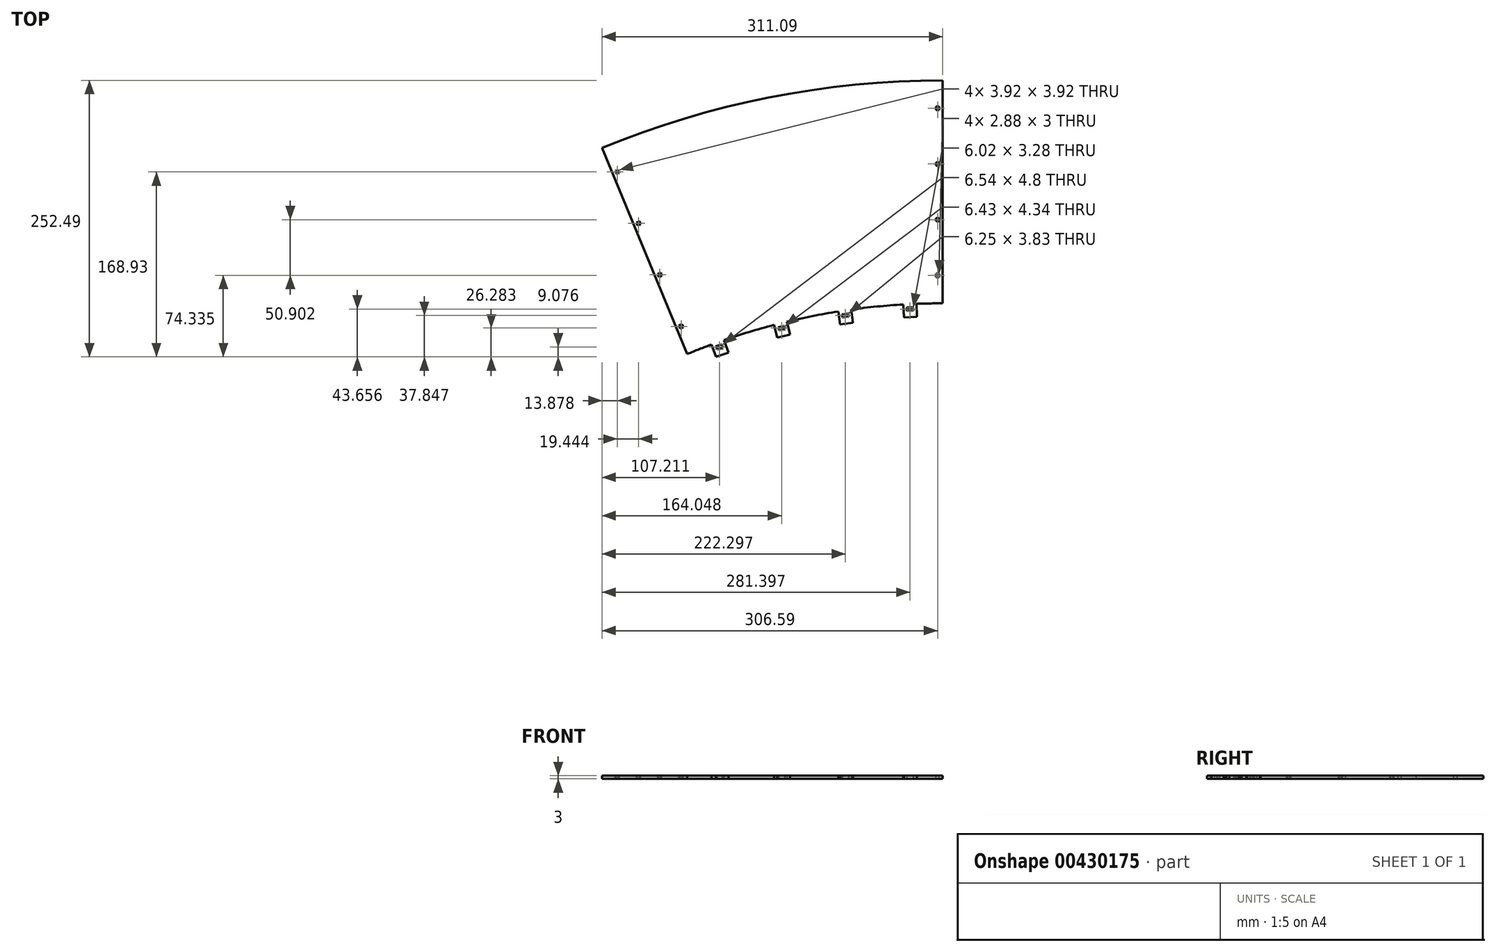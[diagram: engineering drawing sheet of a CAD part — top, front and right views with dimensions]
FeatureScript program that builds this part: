
annotation { "Feature Type Name" : "Feature", "Feature Type Description" : "" }
export const myFeature = defineFeature(function(context is Context, id is Id, definition is map)
    precondition{}
    {
        {
            var Q0;
            Q0=qCreatedBy(makeId("Top.planeOp"),FACE);
            var sketch = newSketch(context, id + "F0", { "sketchPlane" : qUnion([Q0])});
            skLineSegment(sketch, "E0", {"start": v(0, 0) * mm, "end": v(0, 610.8) * mm, "construction": true});
            skLineSegment(sketch, "E1", {"start": v(0, 814.4) * mm, "end": v(0, 610.8) * mm});
            skPoint(sketch, "E2.center", {"position": v(0, 0) * mm});
            skLineSegment(sketch, "E3.1.0", {"start": v(-39.88, 813.42) * mm, "end": v(-29.33, 598.08) * mm, "construction": true});
            skLineSegment(sketch, "E3.anchor2", {"start": v(0, 0) * mm, "end": v(-233.32, 564.48) * mm, "construction": true});
            skArc(sketch, "E4", {"start": v(0, 610.8) * mm, "mid": v(-118.94, 599.1) * mm, "end": v(-233.32, 564.48) * mm});
            skArc(sketch, "E5", {"start": v(0, 814.4) * mm, "mid": v(-158.58, 798.81) * mm, "end": v(-311.1, 752.64) * mm});
            skLineSegment(sketch, "E6.2.2.0", {"start": v(-79.67, 810.5) * mm, "end": v(-59.75, 607.86) * mm, "construction": true});
            skLineSegment(sketch, "E6.2.3.0", {"start": v(-119.27, 805.62) * mm, "end": v(-89.45, 604.2) * mm, "construction": true});
            skLineSegment(sketch, "E6.2.4.0", {"start": v(-158.58, 798.81) * mm, "end": v(-118.94, 599.1) * mm, "construction": true});
            skLineSegment(sketch, "E6.2.5.0", {"start": v(-197.51, 790.09) * mm, "end": v(-148.13, 592.56) * mm, "construction": true});
            skLineSegment(sketch, "E6.2.6.0", {"start": v(-235.97, 779.47) * mm, "end": v(-176.98, 584.6) * mm, "construction": true});
            skLineSegment(sketch, "E6.2.7.0", {"start": v(-273.86, 766.97) * mm, "end": v(-205.4, 575.22) * mm, "construction": true});
            skLineSegment(sketch, "E6.2.8.0", {"start": v(-311.1, 752.64) * mm, "end": v(-233.32, 564.48) * mm});
            skLineSegment(sketch, "E7.bottom", {"start": v(-35.9, 609.77) * mm, "end": v(-23.92, 610.35) * mm});
            skLineSegment(sketch, "E7.top", {"start": v(-35.32, 597.78) * mm, "end": v(-23.33, 598.37) * mm});
            skLineSegment(sketch, "E7.left", {"start": v(-35.9, 609.77) * mm, "end": v(-35.32, 597.78) * mm});
            skLineSegment(sketch, "E7.right", {"start": v(-23.92, 610.35) * mm, "end": v(-23.33, 598.37) * mm});
            skPoint(sketch, "E8.orphan", {"position": v(-29.91, 610.06) * mm});
            skLineSegment(sketch, "E9.bottom", {"start": v(-26.77, 607.21) * mm, "end": v(-32.76, 606.92) * mm, "construction": true});
            skLineSegment(sketch, "E9.top", {"start": v(-26.62, 604.22) * mm, "end": v(-32.62, 603.92) * mm, "construction": true});
            skLineSegment(sketch, "E9.left", {"start": v(-26.77, 607.21) * mm, "end": v(-26.62, 604.22) * mm, "construction": true});
            skLineSegment(sketch, "E9.right", {"start": v(-32.76, 606.92) * mm, "end": v(-32.62, 603.92) * mm, "construction": true});
            skPoint(sketch, "E9.middle", {"position": v(-29.7, 605.57) * mm});
            skLineSegment(sketch, "E10.0", {"start": v(-26.83, 607.2) * mm, "end": v(-26.68, 604.21) * mm});
            skLineSegment(sketch, "E11.0", {"start": v(-32.7, 606.92) * mm, "end": v(-32.55, 603.92) * mm});
            skLineSegment(sketch, "E12", {"start": v(-32.7, 606.92) * mm, "end": v(-26.83, 607.2) * mm});
            skLineSegment(sketch, "E13", {"start": v(-26.68, 604.21) * mm, "end": v(-32.55, 603.92) * mm});
            skLineSegment(sketch, "E14.1.0", {"start": v(-86.1, 601.67) * mm, "end": v(-85.67, 598.7) * mm});
            skPoint(sketch, "E14.1.1", {"position": v(-88.8, 599.76) * mm});
            skPoint(sketch, "E14.1.2", {"position": v(-89.45, 604.2) * mm});
            skLineSegment(sketch, "E14.1.3", {"start": v(-86.05, 601.68) * mm, "end": v(-91.98, 600.8) * mm, "construction": true});
            skLineSegment(sketch, "E14.1.4", {"start": v(-91.92, 600.8) * mm, "end": v(-91.48, 597.84) * mm});
            skLineSegment(sketch, "E14.1.5", {"start": v(-83.52, 605.09) * mm, "end": v(-81.76, 593.22) * mm});
            skLineSegment(sketch, "E14.1.6", {"start": v(-86.05, 601.68) * mm, "end": v(-85.6, 598.71) * mm, "construction": true});
            skLineSegment(sketch, "E14.1.7", {"start": v(-91.92, 600.8) * mm, "end": v(-86.1, 601.67) * mm});
            skLineSegment(sketch, "E14.1.8", {"start": v(-85.6, 598.71) * mm, "end": v(-91.54, 597.83) * mm, "construction": true});
            skLineSegment(sketch, "E14.1.9", {"start": v(-95.39, 603.33) * mm, "end": v(-93.63, 591.46) * mm});
            skLineSegment(sketch, "E14.1.10", {"start": v(-93.63, 591.46) * mm, "end": v(-81.76, 593.22) * mm});
            skLineSegment(sketch, "E14.1.11", {"start": v(-85.67, 598.7) * mm, "end": v(-91.48, 597.84) * mm});
            skLineSegment(sketch, "E14.1.12", {"start": v(-91.98, 600.8) * mm, "end": v(-91.54, 597.83) * mm, "construction": true});
            skLineSegment(sketch, "E14.1.13", {"start": v(-95.39, 603.33) * mm, "end": v(-83.52, 605.09) * mm});
            skLineSegment(sketch, "E14.2.0", {"start": v(-144.55, 590.36) * mm, "end": v(-143.83, 587.45) * mm});
            skPoint(sketch, "E14.2.1", {"position": v(-147.04, 588.2) * mm});
            skPoint(sketch, "E14.2.2", {"position": v(-148.13, 592.56) * mm});
            skLineSegment(sketch, "E14.2.3", {"start": v(-144.5, 590.38) * mm, "end": v(-150.32, 588.92) * mm, "construction": true});
            skLineSegment(sketch, "E14.2.4", {"start": v(-150.26, 588.94) * mm, "end": v(-149.53, 586.02) * mm});
            skLineSegment(sketch, "E14.2.5", {"start": v(-142.31, 594.01) * mm, "end": v(-139.4, 582.37) * mm});
            skLineSegment(sketch, "E14.2.6", {"start": v(-144.5, 590.38) * mm, "end": v(-143.77, 587.47) * mm, "construction": true});
            skLineSegment(sketch, "E14.2.7", {"start": v(-150.26, 588.94) * mm, "end": v(-144.55, 590.36) * mm});
            skLineSegment(sketch, "E14.2.8", {"start": v(-143.77, 587.47) * mm, "end": v(-149.59, 586.01) * mm, "construction": true});
            skLineSegment(sketch, "E14.2.9", {"start": v(-153.95, 591.1) * mm, "end": v(-151.04, 579.46) * mm});
            skLineSegment(sketch, "E14.2.10", {"start": v(-151.04, 579.46) * mm, "end": v(-139.4, 582.37) * mm});
            skLineSegment(sketch, "E14.2.11", {"start": v(-143.83, 587.45) * mm, "end": v(-149.53, 586.02) * mm});
            skLineSegment(sketch, "E14.2.12", {"start": v(-150.32, 588.92) * mm, "end": v(-149.59, 586.01) * mm, "construction": true});
            skLineSegment(sketch, "E14.2.13", {"start": v(-153.95, 591.1) * mm, "end": v(-142.31, 594.01) * mm});
            skLineSegment(sketch, "E14.3.0", {"start": v(-201.62, 573.39) * mm, "end": v(-200.6, 570.56) * mm});
            skPoint(sketch, "E14.3.1", {"position": v(-203.88, 570.99) * mm});
            skPoint(sketch, "E14.3.2", {"position": v(-205.4, 575.22) * mm});
            skLineSegment(sketch, "E14.3.3", {"start": v(-201.56, 573.4) * mm, "end": v(-207.2, 571.4) * mm, "construction": true});
            skLineSegment(sketch, "E14.3.4", {"start": v(-207.15, 571.41) * mm, "end": v(-206.14, 568.59) * mm});
            skLineSegment(sketch, "E14.3.5", {"start": v(-199.74, 577.24) * mm, "end": v(-195.7, 565.94) * mm});
            skLineSegment(sketch, "E14.3.6", {"start": v(-201.56, 573.4) * mm, "end": v(-200.55, 570.58) * mm, "construction": true});
            skLineSegment(sketch, "E14.3.7", {"start": v(-207.15, 571.41) * mm, "end": v(-201.62, 573.39) * mm});
            skLineSegment(sketch, "E14.3.8", {"start": v(-200.55, 570.58) * mm, "end": v(-206.2, 568.56) * mm, "construction": true});
            skLineSegment(sketch, "E14.3.9", {"start": v(-211.04, 573.2) * mm, "end": v(-207, 561.9) * mm});
            skLineSegment(sketch, "E14.3.10", {"start": v(-207, 561.9) * mm, "end": v(-195.7, 565.94) * mm});
            skLineSegment(sketch, "E14.3.11", {"start": v(-200.6, 570.56) * mm, "end": v(-206.14, 568.59) * mm});
            skLineSegment(sketch, "E14.3.12", {"start": v(-207.2, 571.4) * mm, "end": v(-206.2, 568.56) * mm, "construction": true});
            skLineSegment(sketch, "E14.3.13", {"start": v(-211.04, 573.2) * mm, "end": v(-199.74, 577.24) * mm});
            skLineSegment(sketch, "E14.anchor1", {"start": v(0, 0) * mm, "end": v(-35.9, 609.77) * mm, "construction": true});
            skLineSegment(sketch, "E14.anchor2", {"start": v(0, 0) * mm, "end": v(-211.04, 573.2) * mm, "construction": true});
            skSolve(sketch);
        }
        {
            var Q0;
            Q0 = qSketchRegion(id + "F0", true);
            extrude(context, id + "F1", {"entities" : qUnion([Q0]), "depth" : 3 * mm});
        }
        {
            var Q0;
            Q0=makeQuery(id+"F1.opExtrude","CAP_FACE",FACE,{"disambiguationData":[OSD([sQuery(id+"F0.wireOp",EDGE,"E1"),sQuery(id+"F0.wireOp",EDGE,"E4"),sQuery(id+"F0.wireOp",EDGE,"E5"),sQuery(id+"F0.wireOp",EDGE,"E6.2.8.0"),sQuery(id+"F0.wireOp",EDGE,"E7.top"),sQuery(id+"F0.wireOp",EDGE,"E7.left"),sQuery(id+"F0.wireOp",EDGE,"E7.right"),sQuery(id+"F0.wireOp",EDGE,"E10.0"),sQuery(id+"F0.wireOp",EDGE,"E11.0"),sQuery(id+"F0.wireOp",EDGE,"E12"),sQuery(id+"F0.wireOp",EDGE,"E13"),sQuery(id+"F0.wireOp",EDGE,"E14.1.0"),sQuery(id+"F0.wireOp",EDGE,"E14.1.4"),sQuery(id+"F0.wireOp",EDGE,"E14.1.5"),sQuery(id+"F0.wireOp",EDGE,"E14.1.7"),sQuery(id+"F0.wireOp",EDGE,"E14.1.9"),sQuery(id+"F0.wireOp",EDGE,"E14.1.10"),sQuery(id+"F0.wireOp",EDGE,"E14.1.11"),sQuery(id+"F0.wireOp",EDGE,"E14.2.0"),sQuery(id+"F0.wireOp",EDGE,"E14.2.4"),sQuery(id+"F0.wireOp",EDGE,"E14.2.5"),sQuery(id+"F0.wireOp",EDGE,"E14.2.7"),sQuery(id+"F0.wireOp",EDGE,"E14.2.9"),sQuery(id+"F0.wireOp",EDGE,"E14.2.10"),sQuery(id+"F0.wireOp",EDGE,"E14.2.11"),sQuery(id+"F0.wireOp",EDGE,"E14.3.0"),sQuery(id+"F0.wireOp",EDGE,"E14.3.4"),sQuery(id+"F0.wireOp",EDGE,"E14.3.5"),sQuery(id+"F0.wireOp",EDGE,"E14.3.7"),sQuery(id+"F0.wireOp",EDGE,"E14.3.9"),sQuery(id+"F0.wireOp",EDGE,"E14.3.10"),sQuery(id+"F0.wireOp",EDGE,"E14.3.11")])],"isStart":false});
            var sketch = newSketch(context, id + "F2", { "sketchPlane" : qUnion([Q0])});
            skPoint(sketch, "E15", {"position": v(0, 610.8) * mm});
            skPoint(sketch, "E16.0.1.0", {"position": v(0, 636.24) * mm});
            skPoint(sketch, "E16.0.2.0", {"position": v(0, 661.7) * mm});
            skPoint(sketch, "E16.0.3.0", {"position": v(0, 687.15) * mm});
            skPoint(sketch, "E16.0.4.0", {"position": v(0, 712.6) * mm});
            skPoint(sketch, "E16.0.5.0", {"position": v(0, 738.05) * mm});
            skPoint(sketch, "E16.0.6.0", {"position": v(0, 763.5) * mm});
            skPoint(sketch, "E16.0.7.0", {"position": v(0, 788.95) * mm});
            skPoint(sketch, "E16.0.8.0", {"position": v(0, 814.4) * mm});
            skLineSegment(sketch, "E16.direction1", {"start": v(0, 610.8) * mm, "end": v(25.4, 610.8) * mm, "construction": true});
            skLineSegment(sketch, "E16.direction2", {"start": v(0, 610.8) * mm, "end": v(0, 636.24) * mm, "construction": true});
            skLineSegment(sketch, "E17.bottom", {"start": v(-3, 634.74) * mm, "end": v(-6, 634.74) * mm, "construction": true});
            skLineSegment(sketch, "E17.top", {"start": v(-3, 637.74) * mm, "end": v(-6, 637.74) * mm, "construction": true});
            skLineSegment(sketch, "E17.left", {"start": v(-3, 634.74) * mm, "end": v(-3, 637.74) * mm, "construction": true});
            skLineSegment(sketch, "E17.right", {"start": v(-6, 634.74) * mm, "end": v(-6, 637.74) * mm, "construction": true});
            skPoint(sketch, "E17.middle", {"position": v(-4.5, 636.24) * mm});
            skLineSegment(sketch, "E18.bottom", {"start": v(-3.06, 634.74) * mm, "end": v(-5.94, 634.74) * mm});
            skLineSegment(sketch, "E18.top", {"start": v(-3.06, 637.74) * mm, "end": v(-5.94, 637.74) * mm});
            skLineSegment(sketch, "E18.left", {"start": v(-3.06, 634.74) * mm, "end": v(-3.06, 637.74) * mm});
            skLineSegment(sketch, "E18.right", {"start": v(-5.94, 634.74) * mm, "end": v(-5.94, 637.74) * mm});
            skLineSegment(sketch, "E19.0.1.0", {"start": v(-6, 685.65) * mm, "end": v(-6, 688.65) * mm, "construction": true});
            skPoint(sketch, "E19.0.1.1", {"position": v(-4.5, 687.15) * mm});
            skLineSegment(sketch, "E19.0.1.2", {"start": v(-3.06, 685.65) * mm, "end": v(-5.94, 685.65) * mm});
            skPoint(sketch, "E19.0.1.3", {"position": v(-4.5, 687.15) * mm});
            skLineSegment(sketch, "E19.0.1.4", {"start": v(-3, 688.65) * mm, "end": v(-6, 688.65) * mm, "construction": true});
            skLineSegment(sketch, "E19.0.1.5", {"start": v(-3.06, 685.65) * mm, "end": v(-3.06, 688.65) * mm});
            skLineSegment(sketch, "E19.0.1.6", {"start": v(-3.06, 688.65) * mm, "end": v(-5.94, 688.65) * mm});
            skLineSegment(sketch, "E19.0.1.7", {"start": v(-3, 685.65) * mm, "end": v(-6, 685.65) * mm, "construction": true});
            skLineSegment(sketch, "E19.0.1.8", {"start": v(-5.94, 685.65) * mm, "end": v(-5.94, 688.65) * mm});
            skLineSegment(sketch, "E19.0.1.9", {"start": v(-3, 685.65) * mm, "end": v(-3, 688.65) * mm, "construction": true});
            skLineSegment(sketch, "E19.0.2.0", {"start": v(-6, 736.55) * mm, "end": v(-6, 739.55) * mm, "construction": true});
            skPoint(sketch, "E19.0.2.1", {"position": v(-4.5, 738.05) * mm});
            skLineSegment(sketch, "E19.0.2.2", {"start": v(-3.06, 736.55) * mm, "end": v(-5.94, 736.55) * mm});
            skPoint(sketch, "E19.0.2.3", {"position": v(-4.5, 738.05) * mm});
            skLineSegment(sketch, "E19.0.2.4", {"start": v(-3, 739.55) * mm, "end": v(-6, 739.55) * mm, "construction": true});
            skLineSegment(sketch, "E19.0.2.5", {"start": v(-3.06, 736.55) * mm, "end": v(-3.06, 739.55) * mm});
            skLineSegment(sketch, "E19.0.2.6", {"start": v(-3.06, 739.55) * mm, "end": v(-5.94, 739.55) * mm});
            skLineSegment(sketch, "E19.0.2.7", {"start": v(-3, 736.55) * mm, "end": v(-6, 736.55) * mm, "construction": true});
            skLineSegment(sketch, "E19.0.2.8", {"start": v(-5.94, 736.55) * mm, "end": v(-5.94, 739.55) * mm});
            skLineSegment(sketch, "E19.0.2.9", {"start": v(-3, 736.55) * mm, "end": v(-3, 739.55) * mm, "construction": true});
            skLineSegment(sketch, "E19.direction1", {"start": v(-6, 634.74) * mm, "end": v(19.4, 634.74) * mm, "construction": true});
            skLineSegment(sketch, "E19.direction2", {"start": v(-6, 634.74) * mm, "end": v(-6, 685.65) * mm, "construction": true});
            skLineSegment(sketch, "E20.0.0.3", {"start": v(-6, 787.45) * mm, "end": v(-6, 790.45) * mm, "construction": true});
            skPoint(sketch, "E20.3.0.3", {"position": v(-4.5, 788.95) * mm});
            skLineSegment(sketch, "E20.4.0.3", {"start": v(-3.06, 787.45) * mm, "end": v(-5.94, 787.45) * mm});
            skPoint(sketch, "E20.7.0.3", {"position": v(-4.5, 788.95) * mm});
            skLineSegment(sketch, "E20.8.0.3", {"start": v(-3, 790.45) * mm, "end": v(-6, 790.45) * mm, "construction": true});
            skLineSegment(sketch, "E20.11.0.3", {"start": v(-3.06, 787.45) * mm, "end": v(-3.06, 790.45) * mm});
            skLineSegment(sketch, "E20.14.0.3", {"start": v(-3.06, 790.45) * mm, "end": v(-5.94, 790.45) * mm});
            skLineSegment(sketch, "E20.17.0.3", {"start": v(-3, 787.45) * mm, "end": v(-6, 787.45) * mm, "construction": true});
            skLineSegment(sketch, "E20.20.0.3", {"start": v(-5.94, 787.45) * mm, "end": v(-5.94, 790.45) * mm});
            skLineSegment(sketch, "E20.23.0.3", {"start": v(-3, 787.45) * mm, "end": v(-3, 790.45) * mm, "construction": true});
            skLineSegment(sketch, "E21.MirrorCS", {"start": v(3.06, 685.65) * mm, "end": v(5.94, 685.65) * mm});
            skPoint(sketch, "E22.MirrorP", {"position": v(4.5, 687.15) * mm});
            skLineSegment(sketch, "E23.MirrorCS", {"start": v(3.06, 688.65) * mm, "end": v(5.94, 688.65) * mm});
            skLineSegment(sketch, "E24.MirrorCS", {"start": v(5.94, 685.65) * mm, "end": v(5.94, 688.65) * mm});
            skLineSegment(sketch, "E25.MirrorCS", {"start": v(3, 790.45) * mm, "end": v(6, 790.45) * mm});
            skPoint(sketch, "E26.MirrorP", {"position": v(4.5, 738.05) * mm});
            skLineSegment(sketch, "E27.MirrorCS", {"start": v(3, 685.65) * mm, "end": v(3, 688.65) * mm});
            skLineSegment(sketch, "E28.MirrorCS", {"start": v(3, 637.74) * mm, "end": v(6, 637.74) * mm});
            skLineSegment(sketch, "E29.MirrorCS", {"start": v(6, 634.74) * mm, "end": v(6, 637.74) * mm});
            skLineSegment(sketch, "E30.MirrorCS", {"start": v(3.06, 787.45) * mm, "end": v(3.06, 790.45) * mm});
            skLineSegment(sketch, "E31.MirrorCS", {"start": v(3, 736.55) * mm, "end": v(6, 736.55) * mm});
            skLineSegment(sketch, "E32.MirrorCS", {"start": v(3.06, 790.45) * mm, "end": v(5.94, 790.45) * mm});
            skLineSegment(sketch, "E33.MirrorCS", {"start": v(6, 736.55) * mm, "end": v(6, 739.55) * mm});
            skLineSegment(sketch, "E34.MirrorCS", {"start": v(5.94, 736.55) * mm, "end": v(5.94, 739.55) * mm});
            skLineSegment(sketch, "E35.MirrorCS", {"start": v(3, 787.45) * mm, "end": v(6, 787.45) * mm});
            skLineSegment(sketch, "E36.MirrorCS", {"start": v(3.06, 736.55) * mm, "end": v(5.94, 736.55) * mm});
            skLineSegment(sketch, "E37.MirrorCS", {"start": v(3.06, 634.74) * mm, "end": v(3.06, 637.74) * mm});
            skLineSegment(sketch, "E38.MirrorCS", {"start": v(6, 685.65) * mm, "end": v(6, 688.65) * mm});
            skLineSegment(sketch, "E39.MirrorCS", {"start": v(3.06, 685.65) * mm, "end": v(3.06, 688.65) * mm});
            skLineSegment(sketch, "E40.MirrorCS", {"start": v(3, 736.55) * mm, "end": v(3, 739.55) * mm});
            skLineSegment(sketch, "E41.MirrorCS", {"start": v(3, 688.65) * mm, "end": v(6, 688.65) * mm});
            skLineSegment(sketch, "E42.MirrorCS", {"start": v(3, 685.65) * mm, "end": v(6, 685.65) * mm});
            skLineSegment(sketch, "E43.MirrorCS", {"start": v(5.94, 787.45) * mm, "end": v(5.94, 790.45) * mm});
            skLineSegment(sketch, "E44.MirrorCS", {"start": v(3, 739.55) * mm, "end": v(6, 739.55) * mm});
            skPoint(sketch, "E45.MirrorP", {"position": v(4.5, 636.24) * mm});
            skPoint(sketch, "E46.MirrorP", {"position": v(4.5, 788.95) * mm});
            skLineSegment(sketch, "E47.MirrorCS", {"start": v(3, 634.74) * mm, "end": v(6, 634.74) * mm});
            skLineSegment(sketch, "E48.MirrorCS", {"start": v(3, 787.45) * mm, "end": v(3, 790.45) * mm});
            skLineSegment(sketch, "E49.MirrorCS", {"start": v(3.06, 634.74) * mm, "end": v(5.94, 634.74) * mm});
            skLineSegment(sketch, "E50.MirrorCS", {"start": v(3, 634.74) * mm, "end": v(3, 637.74) * mm});
            skLineSegment(sketch, "E51.MirrorCS", {"start": v(3.06, 736.55) * mm, "end": v(3.06, 739.55) * mm});
            skLineSegment(sketch, "E52.MirrorCS", {"start": v(3.06, 739.55) * mm, "end": v(5.94, 739.55) * mm});
            skLineSegment(sketch, "E53.MirrorCS", {"start": v(6, 787.45) * mm, "end": v(6, 790.45) * mm});
            skLineSegment(sketch, "E54.MirrorCS", {"start": v(3.06, 787.45) * mm, "end": v(5.94, 787.45) * mm});
            skLineSegment(sketch, "E55.MirrorCS", {"start": v(3.06, 637.74) * mm, "end": v(5.94, 637.74) * mm});
            skLineSegment(sketch, "E56.MirrorCS", {"start": v(5.94, 634.74) * mm, "end": v(5.94, 637.74) * mm});
            skLineSegment(sketch, "E57.1.0", {"start": v(-259.14, 634.8) * mm, "end": v(-260.28, 637.57) * mm});
            skLineSegment(sketch, "E57.1.1", {"start": v(-279.67, 684.63) * mm, "end": v(-277.01, 685.73) * mm});
            skLineSegment(sketch, "E57.1.2", {"start": v(-260.28, 637.57) * mm, "end": v(-257.51, 638.72) * mm});
            skLineSegment(sketch, "E57.1.3", {"start": v(-259.08, 634.82) * mm, "end": v(-256.42, 635.92) * mm});
            skLineSegment(sketch, "E57.1.4", {"start": v(-260.23, 637.6) * mm, "end": v(-257.57, 638.7) * mm});
            skLineSegment(sketch, "E57.1.5", {"start": v(-298.03, 728.88) * mm, "end": v(-299.17, 731.65) * mm});
            skLineSegment(sketch, "E57.1.6", {"start": v(-239.64, 587.78) * mm, "end": v(-240.78, 590.55) * mm});
            skLineSegment(sketch, "E57.1.7", {"start": v(-240.78, 590.55) * mm, "end": v(-238.12, 591.65) * mm});
            skLineSegment(sketch, "E57.1.8", {"start": v(-279.73, 684.61) * mm, "end": v(-276.95, 685.76) * mm});
            skPoint(sketch, "E57.1.9", {"position": v(-238.88, 589.71) * mm});
            skLineSegment(sketch, "E57.1.10", {"start": v(-278.58, 681.84) * mm, "end": v(-275.8, 682.98) * mm});
            skLineSegment(sketch, "E57.1.11", {"start": v(-278.53, 681.86) * mm, "end": v(-279.67, 684.63) * mm});
            skLineSegment(sketch, "E57.1.12", {"start": v(-278.58, 681.84) * mm, "end": v(-279.73, 684.61) * mm});
            skPoint(sketch, "E57.1.13", {"position": v(-277.77, 683.8) * mm});
            skLineSegment(sketch, "E57.1.14", {"start": v(-239.7, 587.76) * mm, "end": v(-236.92, 588.9) * mm});
            skPoint(sketch, "E57.1.15", {"position": v(-238.88, 589.71) * mm});
            skLineSegment(sketch, "E57.1.16", {"start": v(-275.8, 682.98) * mm, "end": v(-276.95, 685.76) * mm});
            skLineSegment(sketch, "E57.1.17", {"start": v(-295.3, 730) * mm, "end": v(-296.46, 732.78) * mm});
            skLineSegment(sketch, "E57.1.18", {"start": v(-240.84, 590.53) * mm, "end": v(-238.07, 591.67) * mm});
            skLineSegment(sketch, "E57.1.19", {"start": v(-239.7, 587.76) * mm, "end": v(-240.84, 590.53) * mm});
            skLineSegment(sketch, "E57.1.20", {"start": v(-297.97, 728.9) * mm, "end": v(-299.11, 731.68) * mm});
            skLineSegment(sketch, "E57.1.21", {"start": v(-256.42, 635.92) * mm, "end": v(-257.57, 638.7) * mm});
            skPoint(sketch, "E57.1.22", {"position": v(-297.21, 730.84) * mm});
            skLineSegment(sketch, "E57.1.23", {"start": v(-278.53, 681.86) * mm, "end": v(-275.87, 682.96) * mm});
            skLineSegment(sketch, "E57.1.24", {"start": v(-297.97, 728.9) * mm, "end": v(-295.3, 730) * mm});
            skPoint(sketch, "E57.1.25", {"position": v(-277.77, 683.8) * mm});
            skLineSegment(sketch, "E57.1.26", {"start": v(-259.08, 634.82) * mm, "end": v(-260.23, 637.6) * mm});
            skPoint(sketch, "E57.1.27", {"position": v(-297.21, 730.84) * mm});
            skPoint(sketch, "E57.1.28", {"position": v(-258.32, 636.76) * mm});
            skPoint(sketch, "E57.1.29", {"position": v(-258.32, 636.76) * mm});
            skLineSegment(sketch, "E57.1.30", {"start": v(-239.64, 587.78) * mm, "end": v(-236.98, 588.88) * mm});
            skLineSegment(sketch, "E57.1.31", {"start": v(-298.03, 728.88) * mm, "end": v(-295.25, 730.03) * mm});
            skLineSegment(sketch, "E57.1.32", {"start": v(-295.25, 730.03) * mm, "end": v(-296.4, 732.8) * mm});
            skLineSegment(sketch, "E57.1.33", {"start": v(-259.14, 634.8) * mm, "end": v(-256.36, 635.94) * mm});
            skLineSegment(sketch, "E57.1.34", {"start": v(-299.11, 731.68) * mm, "end": v(-296.46, 732.78) * mm});
            skLineSegment(sketch, "E57.1.35", {"start": v(-256.36, 635.94) * mm, "end": v(-257.51, 638.72) * mm});
            skLineSegment(sketch, "E57.1.36", {"start": v(-236.98, 588.88) * mm, "end": v(-238.12, 591.65) * mm});
            skLineSegment(sketch, "E57.1.37", {"start": v(-236.92, 588.9) * mm, "end": v(-238.07, 591.67) * mm});
            skLineSegment(sketch, "E57.1.38", {"start": v(-275.87, 682.96) * mm, "end": v(-277.01, 685.73) * mm});
            skLineSegment(sketch, "E57.1.39", {"start": v(-299.17, 731.65) * mm, "end": v(-296.4, 732.8) * mm});
            skPoint(sketch, "E57.center", {"position": v(0, 0) * mm});
            skLineSegment(sketch, "E57.anchor1", {"start": v(0, 0) * mm, "end": v(3, 634.74) * mm, "construction": true});
            skLineSegment(sketch, "E57.anchor2", {"start": v(0, 0) * mm, "end": v(-239.7, 587.76) * mm, "construction": true});
            skSolve(sketch);
        }
        {
            var Q0;
            Q0 = qSketchRegion(id + "F2", true);
            extrude(context, id + "F3", {"entities" : qUnion([Q0]), "operationType" : NewBodyOperationType.REMOVE, "endBound" : BoundingType.THROUGH_ALL, "oppositeDirection" : true, "depth" : 25.4 * mm});
        }
    });
